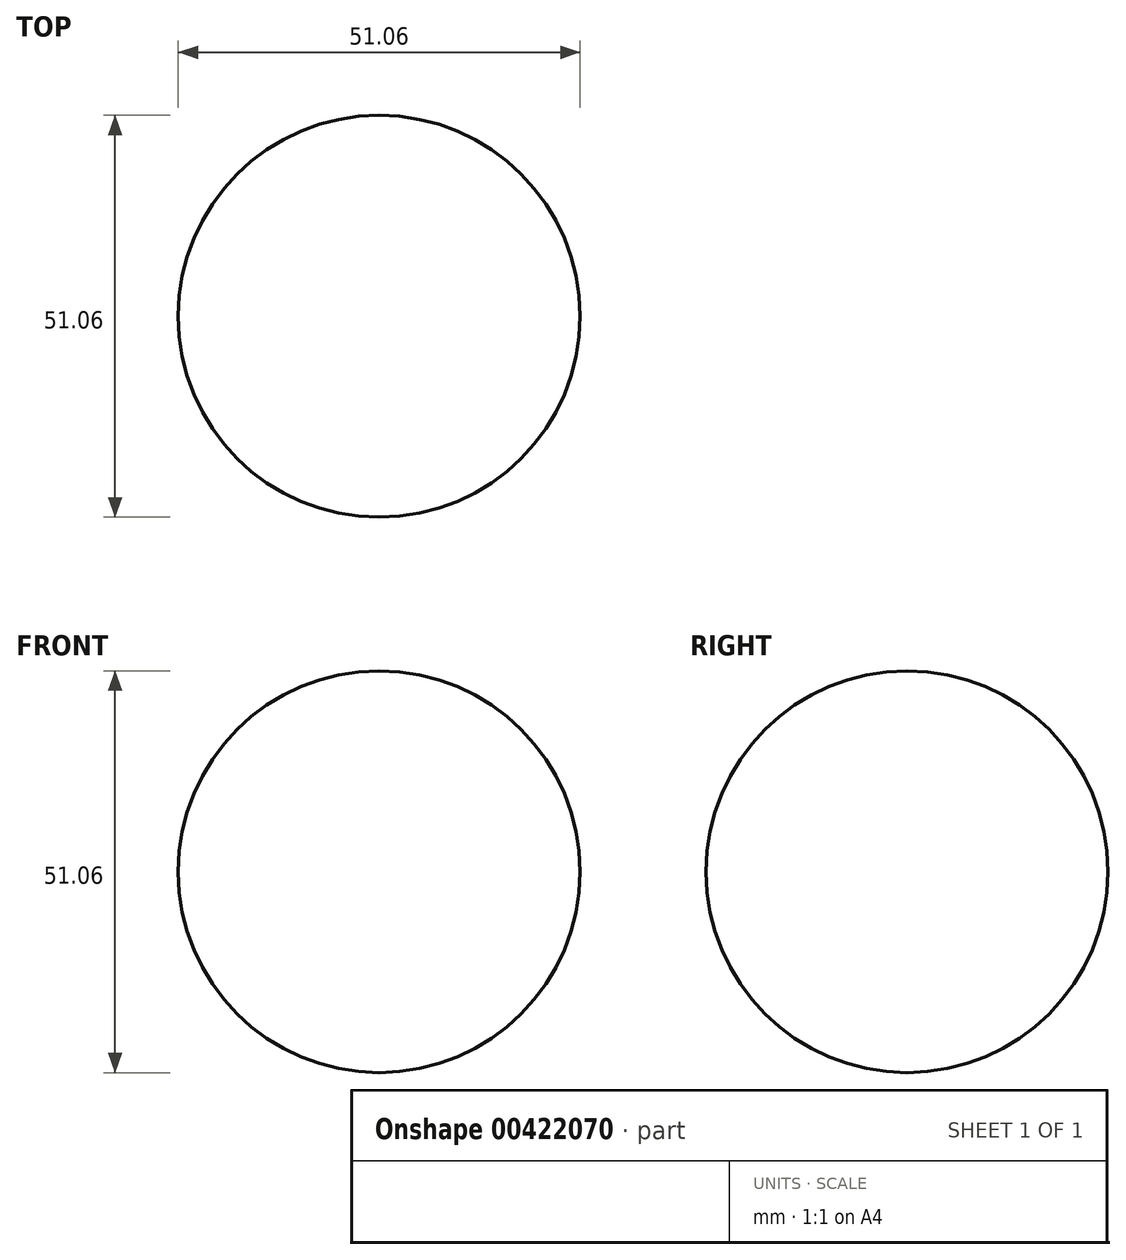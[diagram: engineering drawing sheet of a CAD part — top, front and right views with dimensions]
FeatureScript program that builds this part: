
annotation { "Feature Type Name" : "Feature", "Feature Type Description" : "" }
export const myFeature = defineFeature(function(context is Context, id is Id, definition is map)
    precondition{}
    {
        {
            var Q0;
            Q0=qCreatedBy(makeId("Front.planeOp"),FACE);
            var sketch = newSketch(context, id + "F0", { "sketchPlane" : qUnion([Q0])});
            skArc(sketch, "E0", {"start": v(0, 25.53) * mm, "mid": v(-25.53, 0) * mm, "end": v(0, -25.53) * mm});
            skLineSegment(sketch, "E1", {"start": v(0, 25.53) * mm, "end": v(0, 0) * mm});
            skLineSegment(sketch, "E2", {"start": v(0, 0) * mm, "end": v(0, -25.53) * mm});
            skSolve(sketch);
        }
        {
            var Q0;
            Q0 = qSketchRegion(id + "F0", true);
            var Q1;
            Q1=sQuery(id+"F0.wireOp",EDGE,"E1");
            revolve(context, id + "F1", {"entities" : qUnion([Q0]), "axis" : qUnion([Q1]), "revolveType" : RevolveType.FULL, "oppositeDirection" : true});
        }
    });
